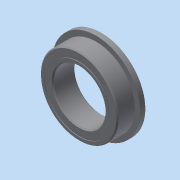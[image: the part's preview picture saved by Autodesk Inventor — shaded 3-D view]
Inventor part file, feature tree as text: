
AUTODESK INVENTOR PART (.ipt)
format: ipt  version: 2015 (Build 190159000, 159)  size: 606,720 bytes
history: native  units: in
note: dims shown in document units (in); Inventor stores cm internally (conversion verified against a paired STEP export)
features: imported_body x16, other x12, revolve x5
ambient origin geometry x8: Origin, YZ Plane, XZ Plane, XY Plane, X Axis, Y Axis, Z Axis, Center Point
bodies: Body1 (feature_tree), Body2 (feature_tree), Body3 (feature_tree), Body4 (feature_tree), Body5 (feature_tree), Body6 (feature_tree), Body7 (feature_tree), Body8 (feature_tree), Body9 (feature_tree), Body10 (feature_tree), Body11 (feature_tree), Body12 (feature_tree), Body13 (feature_tree), Body14 (feature_tree), Body15 (feature_tree), Body16 (feature_tree)
feature tree (33):
  revolve  "Revolve3"  [1 undecoded]
  other  "7804K1451"
  revolve  "Revolve4"  [1 undecoded]
  other  "CirPattern1[1]"
  other  "CirPattern1[2]"
  other  "CirPattern1[3]"
  other  "CirPattern1[4]"
  other  "CirPattern1[5]"
  other  "CirPattern1[6]"
  other  "CirPattern1[7]"
  other  "CirPattern1[8]"
  other  "CirPattern1[9]"
  other  "CirPattern1[10]"
  other  "CirPattern1[11]"
  revolve  "Revolve5[1]"  [1 undecoded]
  revolve  "Revolve5[2]"  [1 undecoded]
  revolve  "Revolve6"  [1 undecoded]
  imported_body  "Base1"
  imported_body  "Base2"
  imported_body  "Base3"
  imported_body  "Base4"
  imported_body  "Base5"
  imported_body  "Base6"
  imported_body  "Base7"
  imported_body  "Base8"
  imported_body  "Base9"
  imported_body  "Base10"
  imported_body  "Base11"
  imported_body  "Base12"
  imported_body  "Base13"
  imported_body  "Base14"
  imported_body  "Base15"
  imported_body  "Base16"
note: 5 required parameter values undecoded (feature->parameter linkage not recoverable at this tier; creation-order binding heuristic only, values carry confidence <= 0.55)
